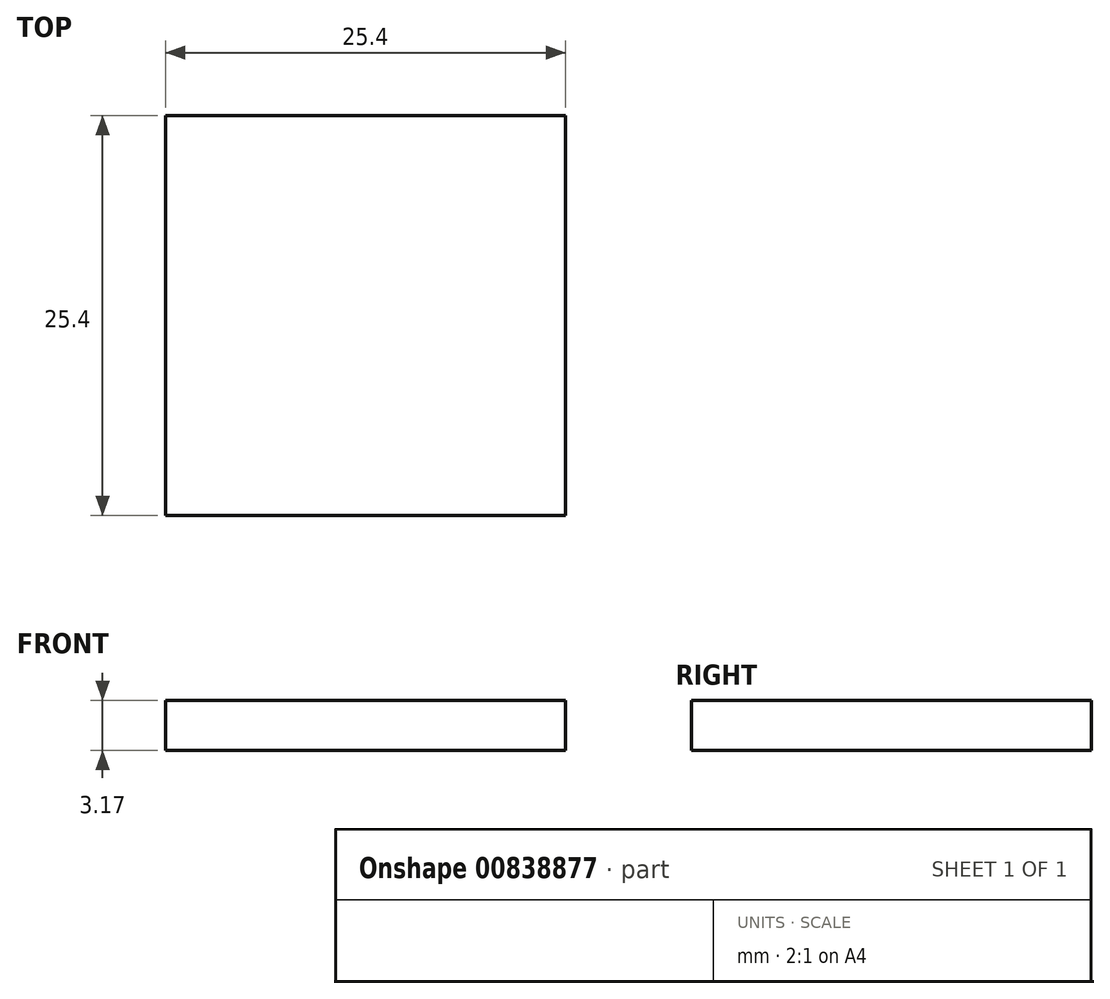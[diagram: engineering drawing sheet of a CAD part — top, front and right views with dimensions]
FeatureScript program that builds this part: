
annotation { "Feature Type Name" : "Feature", "Feature Type Description" : "" }
export const myFeature = defineFeature(function(context is Context, id is Id, definition is map)
    precondition{}
    {
        {
            var Q0;
            Q0=qCreatedBy(makeId("Top.planeOp"),FACE);
            var sketch = newSketch(context, id + "F0", { "sketchPlane" : qUnion([Q0])});
            skLineSegment(sketch, "E0.bottom", {"start": v(12.7, -12.7) * mm, "end": v(-12.7, -12.7) * mm});
            skLineSegment(sketch, "E0.top", {"start": v(12.7, 12.7) * mm, "end": v(-12.7, 12.7) * mm});
            skLineSegment(sketch, "E0.left", {"start": v(12.7, -12.7) * mm, "end": v(12.7, 12.7) * mm});
            skLineSegment(sketch, "E0.right", {"start": v(-12.7, -12.7) * mm, "end": v(-12.7, 12.7) * mm});
            skPoint(sketch, "E0.middle", {"position": v(0, 0) * mm});
            skSolve(sketch);
        }
        {
            var Q0;
            Q0=makeQuery(id+"F0.imprint","IMPRINT",FACE,{"disambiguationData":[TD([[makeQuery(id+"F0.imprint","IMPRINT",EDGE,{"derivedFrom":sQuery(id+"F0.wireOp",EDGE,"E0.bottom")}),-1.0]])]});
            extrude(context, id + "F1", {"entities" : qUnion([Q0]), "depth" : 3.17 * mm, "offsetDistance" : 25.4 * mm});
        }
    });
